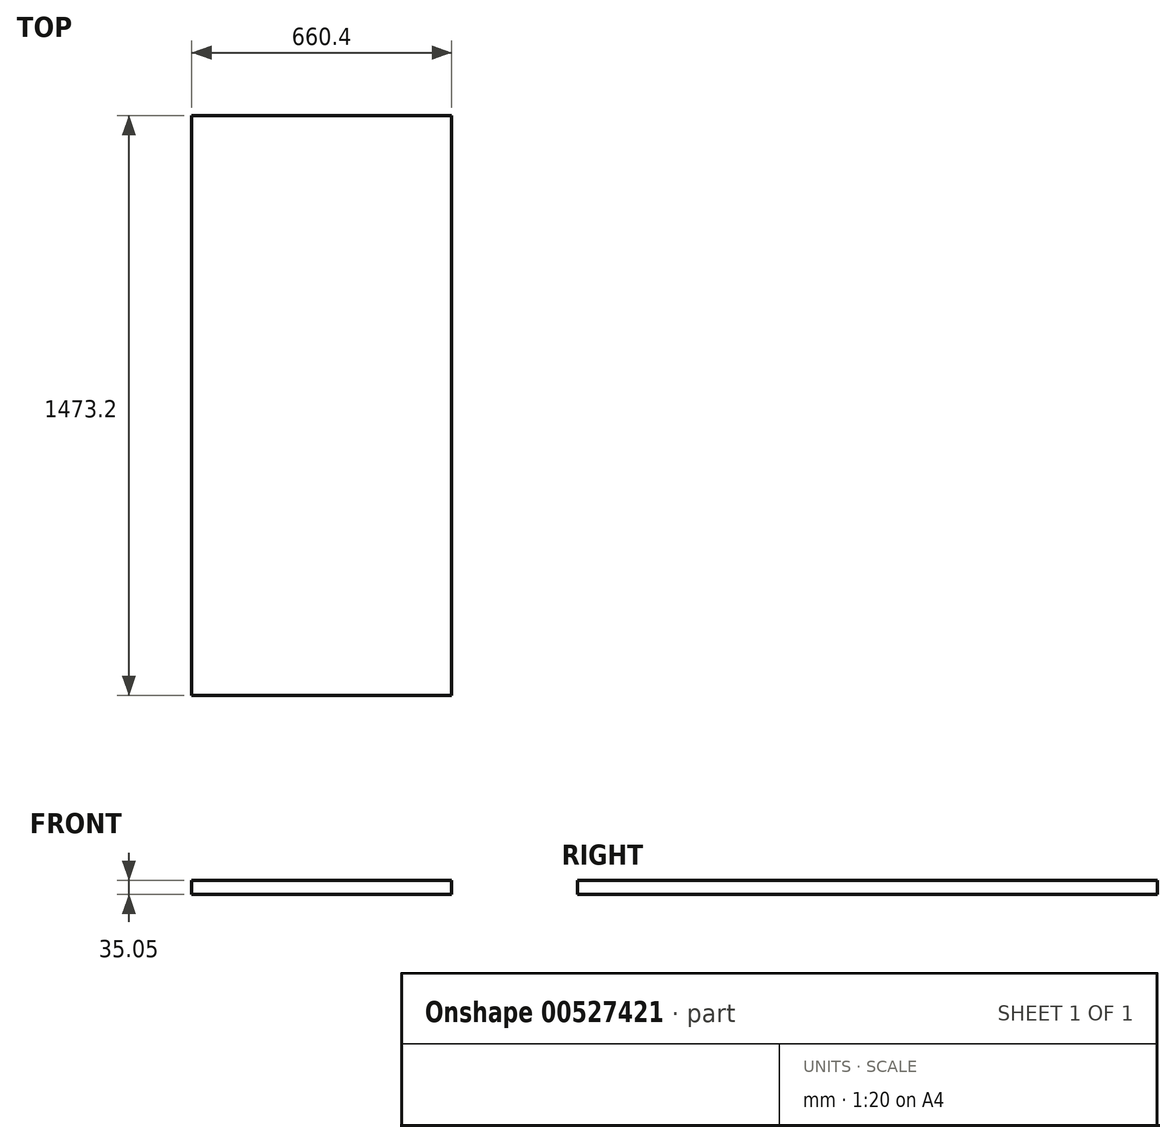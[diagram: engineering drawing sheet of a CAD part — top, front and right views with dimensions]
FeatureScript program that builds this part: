
annotation { "Feature Type Name" : "Feature", "Feature Type Description" : "" }
export const myFeature = defineFeature(function(context is Context, id is Id, definition is map)
    precondition{}
    {
        {
            var Q0;
            Q0=qCreatedBy(makeId("Top.planeOp"),FACE);
            var sketch = newSketch(context, id + "F0", { "sketchPlane" : qUnion([Q0])});
            skLineSegment(sketch, "E0.bottom", {"start": v(-335.46, 881.29) * mm, "end": v(324.94, 881.29) * mm});
            skLineSegment(sketch, "E0.top", {"start": v(-335.46, -591.91) * mm, "end": v(324.94, -591.91) * mm});
            skLineSegment(sketch, "E0.left", {"start": v(-335.46, 881.29) * mm, "end": v(-335.46, -591.91) * mm});
            skLineSegment(sketch, "E0.right", {"start": v(324.94, 881.29) * mm, "end": v(324.94, -591.91) * mm});
            skSolve(sketch);
        }
        {
            var Q0;
            Q0=makeQuery(id+"F0.imprint","IMPRINT",FACE,{"disambiguationData":[TD([[makeQuery(id+"F0.imprint","IMPRINT",EDGE,{"derivedFrom":sQuery(id+"F0.wireOp",EDGE,"E0.bottom")}),-1.0]])]});
            extrude(context, id + "F1", {"entities" : qUnion([Q0]), "depth" : 35.05 * mm, "offsetDistance" : 25.4 * mm});
        }
    });
